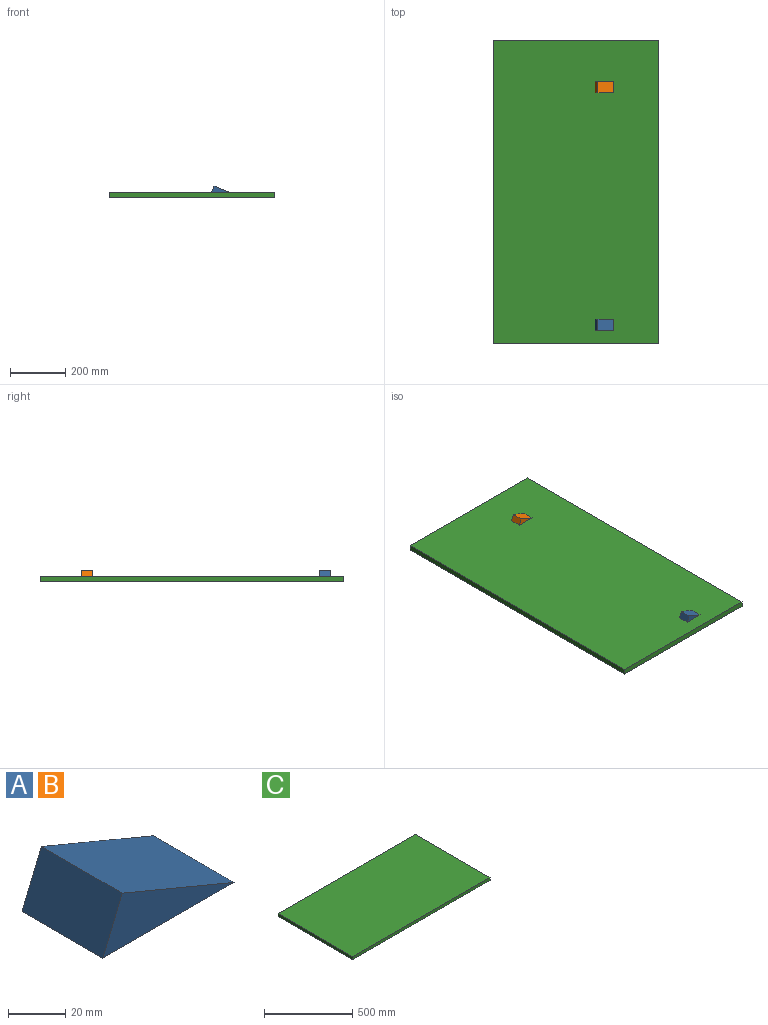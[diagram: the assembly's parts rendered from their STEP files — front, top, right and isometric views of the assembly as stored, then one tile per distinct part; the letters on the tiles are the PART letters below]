
ASSEMBLY  parts=3 mates=2
PART A: 5 faces, bbox 65x40x23.1 mm
  f0: plane 65x40mm, normal (0,0,-1), area 2600mm2, adj f1,f2,f3,f4
  f1: plane 55.38x40mm, normal (0.38,0,0.92), area 2400mm2, adj f0,f2,f3,f4
  f2: plane 40x23.08mm, normal (-0.92,0,0.38), area 1000mm2, adj f0,f1,f3,f4
  f3: plane 65x23.08mm, normal (0,-1,0), area 750mm2, adj f0,f1,f2
  f4: plane 65x23.08mm, normal (0,1,0), area 750mm2, adj f0,f1,f2
PART B: same geometry as A
PART C: 6 faces, bbox 1100x600x20 mm
  f0: plane 600x20mm, normal (1,0,0), area 12000mm2, adj f1,f3,f4,f5
  f1: plane 1100x20mm, normal (0,1,0), area 22000mm2, adj f0,f2,f4,f5
  f2: plane 600x20mm, normal (-1,0,0), area 12000mm2, adj f1,f3,f4,f5
  f3: plane 1100x20mm, normal (0,-1,0), area 22000mm2, adj f0,f2,f4,f5
  f4: plane 1100x600mm, normal (0,0,1), area 660000mm2, adj f0,f1,f2,f3
  f5: plane 1100x600mm, normal (0,0,-1), area 660000mm2, adj f0,f1,f2,f3
PLACE A t=(-212.18,-1406.19,-138.64)mm
PLACE B t=(-212.18,-546.19,-138.64)mm
PLACE C rot(axis=(0.71,0.71,0),180deg) t=(-314.68,-946.19,-151.57)mm
MATE fastened C.f5 <-> B.f0  axis (0,0,-1) through (-244.68,-566.19,-151.57)mm
MATE fastened A.f0 <-> C.f5  axis (0,0,-1) through (-244.68,-1426.19,-151.57)mm
